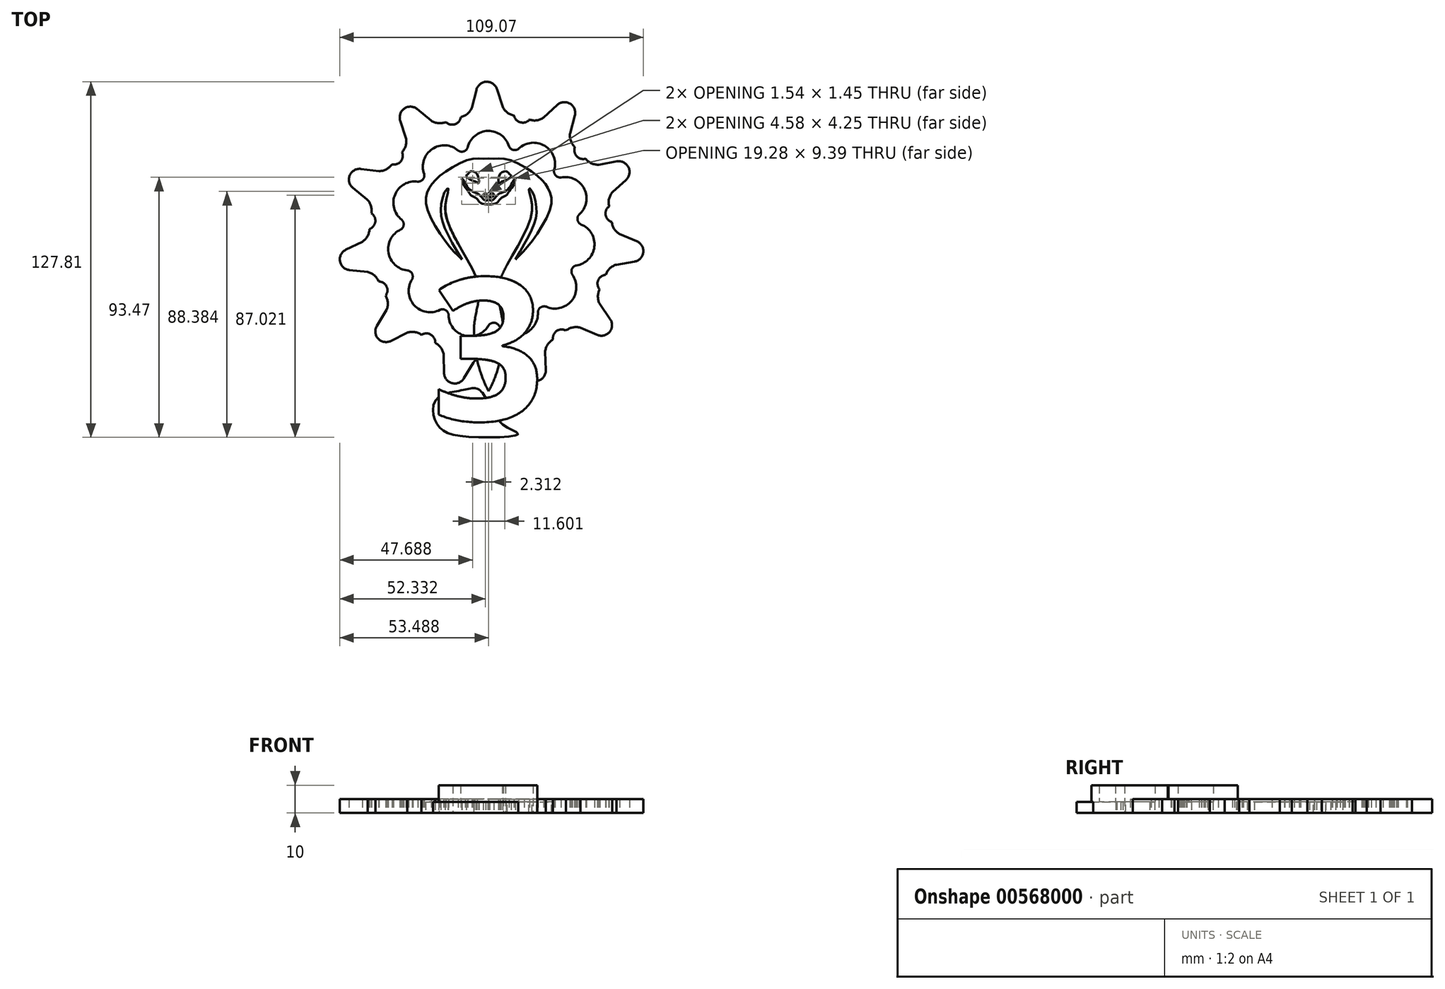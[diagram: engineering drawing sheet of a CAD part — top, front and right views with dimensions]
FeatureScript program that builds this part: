
annotation { "Feature Type Name" : "Feature", "Feature Type Description" : "" }
export const myFeature = defineFeature(function(context is Context, id is Id, definition is map)
    precondition{}
    {
        {
            var Q0;
            Q0=qCreatedBy(makeId("Top.planeOp"),FACE);
            var sketch = newSketch(context, id + "F0", { "sketchPlane" : qUnion([Q0])});
            skArc(sketch, "E0", {"start": v(-109.66, -25.78) * mm, "mid": v(-113.02, -21.98) * mm, "end": v(-117.2, -24.82) * mm});
            skPoint(sketch, "E1.second.point", {"position": v(-122.8, -34.66) * mm});
            skArc(sketch, "E2", {"start": v(-122.8, -34.66) * mm, "mid": v(-120.4, -33.42) * mm, "end": v(-118.85, -31.2) * mm});
            skPoint(sketch, "E2.second.point", {"position": v(-118.85, -31.2) * mm});
            skLineSegment(sketch, "E3", {"start": v(-118.85, -31.2) * mm, "end": v(-117.2, -24.82) * mm});
            skLineSegment(sketch, "E4.anchor1", {"start": v(-112, -77) * mm, "end": v(-113.5, -25.78) * mm, "construction": true});
            skLineSegment(sketch, "E4.anchor2", {"start": v(-112, -77) * mm, "end": v(-113.5, -25.78) * mm, "construction": true});
            skLineSegment(sketch, "E5.MirrorCS", {"start": v(-107.84, -30.88) * mm, "end": v(-109.85, -24.6) * mm});
            skArc(sketch, "E6.MirrorCS", {"start": v(-103.7, -34.1) * mm, "mid": v(-106.17, -33) * mm, "end": v(-107.84, -30.88) * mm});
            skPoint(sketch, "E7.orphan", {"position": v(-118.54, -30) * mm});
            skPoint(sketch, "E8.orphan", {"position": v(-108.22, -29.7) * mm});
            skArc(sketch, "E9.MirrorC", {"start": v(-117.2, -24.82) * mm, "mid": v(-113.6, -21.95) * mm, "end": v(-109.85, -24.6) * mm});
            skCircle(sketch, "E10.MirrorC", {"center": v(-113.5, -25.78) * mm, "radius": 3.83 * mm});
            skArc(sketch, "E11.1.0", {"start": v(-143.98, -47.22) * mm, "mid": v(-142.62, -44.88) * mm, "end": v(-142.52, -42.18) * mm});
            skLineSegment(sketch, "E11.1.1", {"start": v(-142.52, -42.18) * mm, "end": v(-144.6, -35.92) * mm});
            skArc(sketch, "E11.1.2", {"start": v(-144.6, -35.92) * mm, "mid": v(-143.12, -31.56) * mm, "end": v(-138.51, -31.76) * mm});
            skLineSegment(sketch, "E11.1.3", {"start": v(-133.43, -35.95) * mm, "end": v(-138.51, -31.76) * mm});
            skArc(sketch, "E11.1.4", {"start": v(-128.2, -36.42) * mm, "mid": v(-130.88, -36.84) * mm, "end": v(-133.43, -35.95) * mm});
            skArc(sketch, "E11.2.0", {"start": v(-155, -69.23) * mm, "mid": v(-155.13, -66.53) * mm, "end": v(-156.5, -64.2) * mm});
            skLineSegment(sketch, "E11.2.1", {"start": v(-156.5, -64.2) * mm, "end": v(-161.63, -60.06) * mm});
            skArc(sketch, "E11.2.2", {"start": v(-161.63, -60.06) * mm, "mid": v(-162.75, -55.6) * mm, "end": v(-158.76, -53.28) * mm});
            skLineSegment(sketch, "E11.2.3", {"start": v(-152.22, -54.05) * mm, "end": v(-158.76, -53.28) * mm});
            skArc(sketch, "E11.2.4", {"start": v(-147.58, -51.62) * mm, "mid": v(-149.6, -53.42) * mm, "end": v(-152.22, -54.05) * mm});
            skArc(sketch, "E11.3.0", {"start": v(-152.38, -93.71) * mm, "mid": v(-153.94, -91.51) * mm, "end": v(-156.35, -90.3) * mm});
            skLineSegment(sketch, "E11.3.1", {"start": v(-156.35, -90.3) * mm, "end": v(-162.9, -89.58) * mm});
            skArc(sketch, "E11.3.2", {"start": v(-162.9, -89.58) * mm, "mid": v(-166.26, -86.43) * mm, "end": v(-164.16, -82.33) * mm});
            skLineSegment(sketch, "E11.3.3", {"start": v(-158.24, -79.44) * mm, "end": v(-164.16, -82.33) * mm});
            skArc(sketch, "E11.3.4", {"start": v(-155.65, -74.89) * mm, "mid": v(-156.38, -77.49) * mm, "end": v(-158.24, -79.44) * mm});
            skArc(sketch, "E11.4.0", {"start": v(-136.93, -112.89) * mm, "mid": v(-139.44, -111.88) * mm, "end": v(-142.12, -112.17) * mm});
            skLineSegment(sketch, "E11.4.1", {"start": v(-142.12, -112.17) * mm, "end": v(-148.02, -115.1) * mm});
            skArc(sketch, "E11.4.2", {"start": v(-148.02, -115.1) * mm, "mid": v(-152.55, -114.27) * mm, "end": v(-153, -109.68) * mm});
            skLineSegment(sketch, "E11.4.3", {"start": v(-149.58, -104.05) * mm, "end": v(-153, -109.68) * mm});
            skArc(sketch, "E11.4.4", {"start": v(-149.86, -98.82) * mm, "mid": v(-149.07, -101.4) * mm, "end": v(-149.58, -104.05) * mm});
            skArc(sketch, "E11.5.0", {"start": v(-113.57, -120.67) * mm, "mid": v(-116.22, -121.18) * mm, "end": v(-118.33, -122.87) * mm});
            skLineSegment(sketch, "E11.5.1", {"start": v(-118.33, -122.87) * mm, "end": v(-121.7, -128.53) * mm});
            skArc(sketch, "E11.5.2", {"start": v(-121.7, -128.53) * mm, "mid": v(-125.97, -130.28) * mm, "end": v(-128.83, -126.66) * mm});
            skLineSegment(sketch, "E11.5.3", {"start": v(-128.99, -120.08) * mm, "end": v(-128.83, -126.66) * mm});
            skArc(sketch, "E11.5.4", {"start": v(-132.06, -115.83) * mm, "mid": v(-130, -117.57) * mm, "end": v(-128.99, -120.08) * mm});
            skArc(sketch, "E11.6.0", {"start": v(-89.71, -114.59) * mm, "mid": v(-91.67, -116.45) * mm, "end": v(-92.52, -119.01) * mm});
            skLineSegment(sketch, "E11.6.1", {"start": v(-92.52, -119.01) * mm, "end": v(-92.3, -125.6) * mm});
            skArc(sketch, "E11.6.2", {"start": v(-92.3, -125.6) * mm, "mid": v(-94.95, -129.37) * mm, "end": v(-99.3, -127.88) * mm});
            skLineSegment(sketch, "E11.6.3", {"start": v(-103, -122.42) * mm, "end": v(-99.3, -127.88) * mm});
            skArc(sketch, "E11.6.4", {"start": v(-107.88, -120.5) * mm, "mid": v(-105.2, -120.86) * mm, "end": v(-103, -122.42) * mm});
            skArc(sketch, "E11.7.0", {"start": v(-72.93, -96.57) * mm, "mid": v(-73.57, -99.2) * mm, "end": v(-72.9, -101.81) * mm});
            skLineSegment(sketch, "E11.7.1", {"start": v(-72.9, -101.81) * mm, "end": v(-69.16, -107.23) * mm});
            skArc(sketch, "E11.7.2", {"start": v(-69.16, -107.23) * mm, "mid": v(-69.34, -111.83) * mm, "end": v(-73.81, -112.94) * mm});
            skLineSegment(sketch, "E11.7.3", {"start": v(-79.87, -110.35) * mm, "end": v(-73.81, -112.94) * mm});
            skArc(sketch, "E11.7.4", {"start": v(-85.01, -111.37) * mm, "mid": v(-82.57, -110.22) * mm, "end": v(-79.87, -110.35) * mm});
            skArc(sketch, "E11.8.0", {"start": v(-68.55, -72.34) * mm, "mid": v(-67.67, -74.9) * mm, "end": v(-65.7, -76.74) * mm});
            skLineSegment(sketch, "E11.8.1", {"start": v(-65.7, -76.74) * mm, "end": v(-59.61, -79.27) * mm});
            skArc(sketch, "E11.8.2", {"start": v(-59.61, -79.27) * mm, "mid": v(-57.28, -83.24) * mm, "end": v(-60.45, -86.59) * mm});
            skLineSegment(sketch, "E11.8.3", {"start": v(-66.94, -87.69) * mm, "end": v(-60.45, -86.59) * mm});
            skArc(sketch, "E11.8.4", {"start": v(-70.72, -91.33) * mm, "mid": v(-69.28, -89.04) * mm, "end": v(-66.94, -87.69) * mm});
            skArc(sketch, "E11.9.0", {"start": v(-77.97, -49.59) * mm, "mid": v(-75.85, -51.26) * mm, "end": v(-73.19, -51.74) * mm});
            skLineSegment(sketch, "E11.9.1", {"start": v(-73.19, -51.74) * mm, "end": v(-66.7, -50.59) * mm});
            skArc(sketch, "E11.9.2", {"start": v(-66.7, -50.59) * mm, "mid": v(-62.6, -52.67) * mm, "end": v(-63.45, -57.2) * mm});
            skLineSegment(sketch, "E11.9.3", {"start": v(-68.32, -61.63) * mm, "end": v(-63.45, -57.2) * mm});
            skArc(sketch, "E11.9.4", {"start": v(-69.52, -66.73) * mm, "mid": v(-69.56, -64.03) * mm, "end": v(-68.32, -61.63) * mm});
            skArc(sketch, "E11.10.0", {"start": v(-98.2, -35.54) * mm, "mid": v(-95.5, -35.8) * mm, "end": v(-93, -34.77) * mm});
            skLineSegment(sketch, "E11.10.1", {"start": v(-93, -34.77) * mm, "end": v(-88.17, -30.3) * mm});
            skArc(sketch, "E11.10.2", {"start": v(-88.17, -30.3) * mm, "mid": v(-83.6, -29.82) * mm, "end": v(-81.86, -34.09) * mm});
            skLineSegment(sketch, "E11.10.3", {"start": v(-83.56, -40.45) * mm, "end": v(-81.86, -34.09) * mm});
            skArc(sketch, "E11.10.4", {"start": v(-81.82, -45.4) * mm, "mid": v(-83.3, -43.14) * mm, "end": v(-83.56, -40.45) * mm});
            skPoint(sketch, "E11.center", {"position": v(-112, -77) * mm});
            skArc(sketch, "E12", {"start": v(-103.7, -34.1) * mm, "mid": v(-101.4, -36.54) * mm, "end": v(-98.2, -35.54) * mm});
            skArc(sketch, "E13.1.0", {"start": v(-128.2, -36.42) * mm, "mid": v(-124.95, -37.23) * mm, "end": v(-122.8, -34.66) * mm});
            skArc(sketch, "E13.2.0", {"start": v(-147.58, -51.62) * mm, "mid": v(-144.4, -50.54) * mm, "end": v(-143.98, -47.22) * mm});
            skArc(sketch, "E13.3.0", {"start": v(-155.65, -74.89) * mm, "mid": v(-153.56, -72.26) * mm, "end": v(-155, -69.23) * mm});
            skArc(sketch, "E13.4.0", {"start": v(-149.86, -98.82) * mm, "mid": v(-149.52, -95.48) * mm, "end": v(-152.38, -93.71) * mm});
            skArc(sketch, "E13.5.0", {"start": v(-132.06, -115.83) * mm, "mid": v(-133.58, -112.83) * mm, "end": v(-136.93, -112.89) * mm});
            skArc(sketch, "E13.6.0", {"start": v(-107.88, -120.5) * mm, "mid": v(-110.78, -118.8) * mm, "end": v(-113.57, -120.67) * mm});
            skArc(sketch, "E13.7.0", {"start": v(-85.01, -111.37) * mm, "mid": v(-88.37, -111.51) * mm, "end": v(-89.71, -114.59) * mm});
            skArc(sketch, "E13.8.0", {"start": v(-70.72, -91.33) * mm, "mid": v(-73.46, -93.26) * mm, "end": v(-72.93, -96.57) * mm});
            skArc(sketch, "E13.9.0", {"start": v(-69.52, -66.73) * mm, "mid": v(-70.79, -69.84) * mm, "end": v(-68.55, -72.34) * mm});
            skArc(sketch, "E13.10.0", {"start": v(-81.82, -45.4) * mm, "mid": v(-81.2, -48.7) * mm, "end": v(-77.97, -49.59) * mm});
            skCircle(sketch, "E14", {"center": v(-112.87, -47.3) * mm, "radius": 7.68 * mm});
            skCircle(sketch, "E15.1.0", {"center": v(-128.8, -52.48) * mm, "radius": 7.68 * mm});
            skCircle(sketch, "E15.2.0", {"center": v(-139.38, -65.45) * mm, "radius": 7.68 * mm});
            skCircle(sketch, "E15.3.0", {"center": v(-141.28, -82.09) * mm, "radius": 7.68 * mm});
            skCircle(sketch, "E15.4.0", {"center": v(-133.88, -97.11) * mm, "radius": 7.68 * mm});
            skCircle(sketch, "E15.5.0", {"center": v(-119.54, -105.75) * mm, "radius": 7.68 * mm});
            skCircle(sketch, "E15.6.0", {"center": v(-102.8, -105.26) * mm, "radius": 7.68 * mm});
            skCircle(sketch, "E15.7.0", {"center": v(-88.98, -95.8) * mm, "radius": 7.68 * mm});
            skCircle(sketch, "E15.8.0", {"center": v(-82.47, -80.37) * mm, "radius": 7.68 * mm});
            skCircle(sketch, "E15.9.0", {"center": v(-85.34, -63.87) * mm, "radius": 7.68 * mm});
            skCircle(sketch, "E15.10.0", {"center": v(-96.67, -51.54) * mm, "radius": 7.68 * mm});
            skArc(sketch, "E16", {"start": v(-105.62, -44.76) * mm, "mid": v(-104.03, -46.44) * mm, "end": v(-101.8, -45.83) * mm});
            skArc(sketch, "E17.1.0", {"start": v(-124.06, -46.43) * mm, "mid": v(-121.82, -46.99) * mm, "end": v(-120.28, -45.27) * mm});
            skArc(sketch, "E17.2.0", {"start": v(-138.67, -57.8) * mm, "mid": v(-136.49, -57.06) * mm, "end": v(-136.12, -54.78) * mm});
            skArc(sketch, "E17.3.0", {"start": v(-144.82, -75.27) * mm, "mid": v(-143.38, -73.46) * mm, "end": v(-144.3, -71.35) * mm});
            skArc(sketch, "E17.4.0", {"start": v(-140.54, -93.29) * mm, "mid": v(-140.31, -90.99) * mm, "end": v(-142.23, -89.7) * mm});
            skArc(sketch, "E17.5.0", {"start": v(-127.2, -106.13) * mm, "mid": v(-128.25, -104.07) * mm, "end": v(-130.56, -104.04) * mm});
            skArc(sketch, "E17.6.0", {"start": v(-109.04, -109.73) * mm, "mid": v(-111.03, -108.56) * mm, "end": v(-113, -109.78) * mm});
            skArc(sketch, "E17.7.0", {"start": v(-91.82, -102.93) * mm, "mid": v(-94.12, -103.03) * mm, "end": v(-95.12, -105.12) * mm});
            skArc(sketch, "E17.8.0", {"start": v(-81, -87.9) * mm, "mid": v(-82.89, -89.23) * mm, "end": v(-82.6, -91.53) * mm});
            skArc(sketch, "E17.9.0", {"start": v(-80.02, -69.41) * mm, "mid": v(-80.9, -71.55) * mm, "end": v(-79.41, -73.32) * mm});
            skArc(sketch, "E17.10.0", {"start": v(-89.2, -53.33) * mm, "mid": v(-88.78, -55.6) * mm, "end": v(-86.57, -56.29) * mm});
            skSolve(sketch);
        }
        {
            var Q0;
            {var subQ56=sQuery(id+"F0.wireOp",EDGE,"E5.MirrorCS");Q0=makeQuery(id+"F0.imprint","IMPRINT",FACE,{"disambiguationData":[TD([[makeQuery(id+"F0.imprint","IMPRINT",EDGE,{"derivedFrom":subQ56}),1.0]])]});}
            var Q1;
            {var subQ0=sQuery(id+"F0.wireOp",EDGE,"E10.MirrorC");var subQ2=makeQuery(id+"F0.imprint","IMPRINT",VERTEX,{"derivedFrom":subQ0});Q1=makeQuery(id+"F0.imprint","IMPRINT",FACE,{"disambiguationData":[TD([[makeQuery(id+"F0.imprint","IMPRINT",EDGE,{"disambiguationData":[TD([[subQ2,-1.0]])],"derivedFrom":subQ0}),1.0]])]});}
            extrude(context, id + "F1", {"entities" : qUnion([Q0, Q1]), "depth" : 5 * mm, "offsetDistance" : 25 * mm});
        }
        {
            var Q0;
            Q0=qCreatedBy(makeId("Top.planeOp"),FACE);
            var sketch = newSketch(context, id + "F2", { "sketchPlane" : qUnion([Q0])});
            skFitSpline(sketch, "E18", {"points": [v(-112.83, -49.51) * mm, v(-118.74, -49.63) * mm, v(-129.75, -55.3) * mm, v(-134.18, -60.18) * mm, v(-135.31, -66.2) * mm, v(-128.04, -79.7) * mm, v(-122.41, -85.87) * mm], "startDerivative": vector(-43.86, -6.07) * mm, "endDerivative": vector(32.46, -31.67) * mm});
            skFitSpline(sketch, "E19", {"points": [v(-122.41, -85.87) * mm, v(-128.82, -73.98) * mm, v(-130.03, -67.9) * mm, v(-128.74, -61.85) * mm, v(-127.4, -60.21) * mm, v(-127.69, -62.6) * mm, v(-128.1, -70.35) * mm, v(-119.13, -88.38) * mm, v(-116.18, -98.1) * mm, v(-118.08, -110.57) * mm, v(-114.08, -130.66) * mm, v(-104.12, -143.67) * mm], "startDerivative": vector(-71.17, 119.07) * mm, "endDerivative": vector(113.09, -113.09) * mm});
            skLineSegment(sketch, "E20", {"start": v(-112.83, -49.51) * mm, "end": v(-112.83, -58.45) * mm});
            skFitSpline(sketch, "E21", {"points": [v(-104.12, -143.67) * mm, v(-93.53, -149.06) * mm, v(-72.24, -147.82) * mm, v(-65.43, -143.67) * mm, v(-63.08, -140.89) * mm, v(-64.69, -133.46) * mm, v(-71.62, -132.22) * mm, v(-85.6, -133.21) * mm, v(-97.25, -131.73) * mm], "startDerivative": vector(64.94, -48) * mm, "endDerivative": vector(-82.53, 15.68) * mm});
            skFitSpline(sketch, "E22", {"points": [v(-97.25, -131.73) * mm, v(-93.16, -135.2) * mm, v(-85.49, -138.66) * mm], "startDerivative": vector(8.19, -8.16) * mm, "endDerivative": vector(15.08, -5.8) * mm});
            skFitSpline(sketch, "E23", {"points": [v(-85.49, -138.66) * mm, v(-89.82, -138.66) * mm, v(-98.36, -133.21) * mm, v(-105.17, -121.95) * mm, v(-107.4, -108.82) * mm, v(-106.78, -98.67) * mm], "startDerivative": vector(-30.27, -4.72) * mm, "endDerivative": vector(5.19, 48.18) * mm});
            skFitSpline(sketch, "E24", {"points": [v(-116.38, -132.5) * mm, v(-111.8, -139.85) * mm, v(-106.55, -145.96) * mm, v(-102.25, -148.63) * mm, v(-120.58, -149.5) * mm, v(-130.03, -146.63) * mm, v(-132.7, -141.28) * mm, v(-131.08, -135.46) * mm, v(-121.73, -132.69) * mm, v(-116.38, -132.5) * mm]});
            skFitSpline(sketch, "E25.MirrorCS", {"points": [v(-112.83, -49.51) * mm, v(-106.93, -49.63) * mm, v(-95.92, -55.3) * mm, v(-91.49, -60.18) * mm, v(-90.35, -66.2) * mm, v(-97.62, -79.7) * mm, v(-103.25, -85.87) * mm], "startDerivative": vector(43.86, -6.07) * mm, "endDerivative": vector(-32.46, -31.67) * mm});
            skFitSpline(sketch, "E26.MirrorCS", {"points": [v(-103.25, -85.87) * mm, v(-96.84, -73.98) * mm, v(-95.63, -67.9) * mm, v(-96.93, -61.85) * mm, v(-98.25, -60.21) * mm, v(-97.97, -62.6) * mm, v(-97.56, -70.35) * mm, v(-106.53, -88.38) * mm, v(-109.48, -98.1) * mm, v(-107.58, -110.57) * mm, v(-111.58, -130.66) * mm, v(-121.54, -143.67) * mm], "startDerivative": vector(71.17, 119.07) * mm, "endDerivative": vector(-113.09, -113.09) * mm});
            skFitSpline(sketch, "E27", {"points": [v(-106.1, -87.6) * mm, v(-107.32, -92.14) * mm, v(-106.88, -96.07) * mm, v(-106.78, -98.67) * mm], "startDerivative": vector(-6.51, -10.37) * mm, "endDerivative": vector(-0.47, -8.6) * mm});
            skFitSpline(sketch, "E28", {"points": [v(-120.92, -55.8) * mm, v(-120.32, -55.2) * mm, v(-119.65, -54.35) * mm, v(-117.15, -54.81) * mm, v(-116.48, -58.44) * mm, v(-117.08, -58.09) * mm, v(-118.77, -57.46) * mm, v(-120.92, -55.8) * mm]});
            skFitSpline(sketch, "E29", {"points": [v(-122.47, -56.68) * mm, v(-121.6, -59.4) * mm, v(-119.97, -61.58) * mm, v(-119.16, -62.81) * mm, v(-117.64, -63.52) * mm, v(-116.4, -64.75) * mm, v(-115.35, -65.7) * mm, v(-112.29, -66.1) * mm, v(-111.09, -66.13) * mm], "startDerivative": vector(4, -18.73) * mm, "endDerivative": vector(10.1, -0.3) * mm});
            skFitSpline(sketch, "E30", {"points": [v(-122.47, -56.68) * mm, v(-121.7, -57.5) * mm, v(-120.7, -59.32) * mm, v(-118.8, -61.33) * mm, v(-116.8, -62.1) * mm, v(-115.56, -63.17) * mm, v(-114.72, -64.19) * mm, v(-113.7, -64.65) * mm, v(-112.92, -64.33) * mm], "startDerivative": vector(7.67, -6.61) * mm, "endDerivative": vector(8.03, 5.14) * mm});
            skFitSpline(sketch, "E31", {"points": [v(-114.52, -62.24) * mm, v(-114.69, -62.87) * mm, v(-113.26, -63.46) * mm, v(-113.7, -62.1) * mm, v(-114.52, -62.24) * mm]});
            skFitSpline(sketch, "E32.MirrorC", {"points": [v(-111.14, -62.24) * mm, v(-110.98, -62.87) * mm, v(-112.4, -63.46) * mm, v(-111.95, -62.1) * mm, v(-111.14, -62.24) * mm]});
            skFitSpline(sketch, "E33.MirrorC", {"points": [v(-104.74, -55.8) * mm, v(-105.34, -55.2) * mm, v(-106.01, -54.35) * mm, v(-108.51, -54.81) * mm, v(-109.18, -58.44) * mm, v(-108.58, -58.09) * mm, v(-106.9, -57.46) * mm, v(-104.74, -55.8) * mm]});
            skFitSpline(sketch, "E34.MirrorCS", {"points": [v(-103.2, -56.68) * mm, v(-103.97, -57.5) * mm, v(-104.95, -59.32) * mm, v(-106.86, -61.33) * mm, v(-108.87, -62.1) * mm, v(-110.1, -63.17) * mm, v(-110.95, -64.19) * mm, v(-111.97, -64.65) * mm, v(-112.74, -64.33) * mm], "startDerivative": vector(-7.67, -6.61) * mm, "endDerivative": vector(-8.03, 5.14) * mm});
            skFitSpline(sketch, "E35.MirrorCS", {"points": [v(-103.2, -56.68) * mm, v(-104.07, -59.4) * mm, v(-105.7, -61.58) * mm, v(-106.5, -62.81) * mm, v(-108.02, -63.52) * mm, v(-109.25, -64.75) * mm, v(-110.31, -65.7) * mm, v(-113.38, -66.1) * mm, v(-114.58, -66.13) * mm], "startDerivative": vector(-4, -18.73) * mm, "endDerivative": vector(-10.1, -0.3) * mm});
            skFitSpline(sketch, "E36", {"points": [v(-112.92, -64.33) * mm, v(-112.85, -64.28) * mm, v(-112.74, -64.33) * mm], "startDerivative": vector(0.15, 0.16) * mm, "endDerivative": vector(0.2, -0.16) * mm});
            skSolve(sketch);
        }
        {
            var Q0;
            Q0=makeQuery(id+"F2.imprint","IMPRINT",FACE,{"disambiguationData":[TD([[makeQuery(id+"F2.imprint","IMPRINT",EDGE,{"derivedFrom":sQuery(id+"F2.wireOp",EDGE,"E18")}),1.0]])]});
            var Q1;
            Q1=makeQuery(id+"F2.imprint","IMPRINT",FACE,{"disambiguationData":[TD([[makeQuery(id+"F2.imprint","IMPRINT",EDGE,{"derivedFrom":sQuery(id+"F2.wireOp",EDGE,"E24")}),-1.0]])]});
            extrude(context, id + "F3", {"entities" : qUnion([Q0, Q1]), "operationType" : NewBodyOperationType.ADD, "depth" : 4 * mm, "offsetDistance" : 25 * mm});
        }
        {
            var Q0;
            Q0=qCreatedBy(makeId("Top.planeOp"),FACE);
            var sketch = newSketch(context, id + "F4", { "sketchPlane" : qUnion([Q0])});
            skText(sketch, "E37", { "text": "3", "fontName": "OpenSans-Bold.ttf"});
            const initialGuessF4  = {"E37": [-0.13349, -0.14366, 1, 0, 0.05155]};
            skSetInitialGuess(sketch, initialGuessF4);
            skSolve(sketch);
        }
        {
            var Q0;
            Q0=makeQuery(id+"F4.imprint","IMPRINT",FACE,{"disambiguationData":[TD([[makeQuery(id+"F4.imprint","IMPRINT",EDGE,{"derivedFrom":sQuery(id+"F4.wireOp",EDGE,"E37.sketch_text.stroke-0")}),-1.0]])]});
            extrude(context, id + "F5", {"entities" : qUnion([Q0]), "operationType" : NewBodyOperationType.ADD, "depth" : 10 * mm, "offsetDistance" : 25 * mm});
        }
    });
